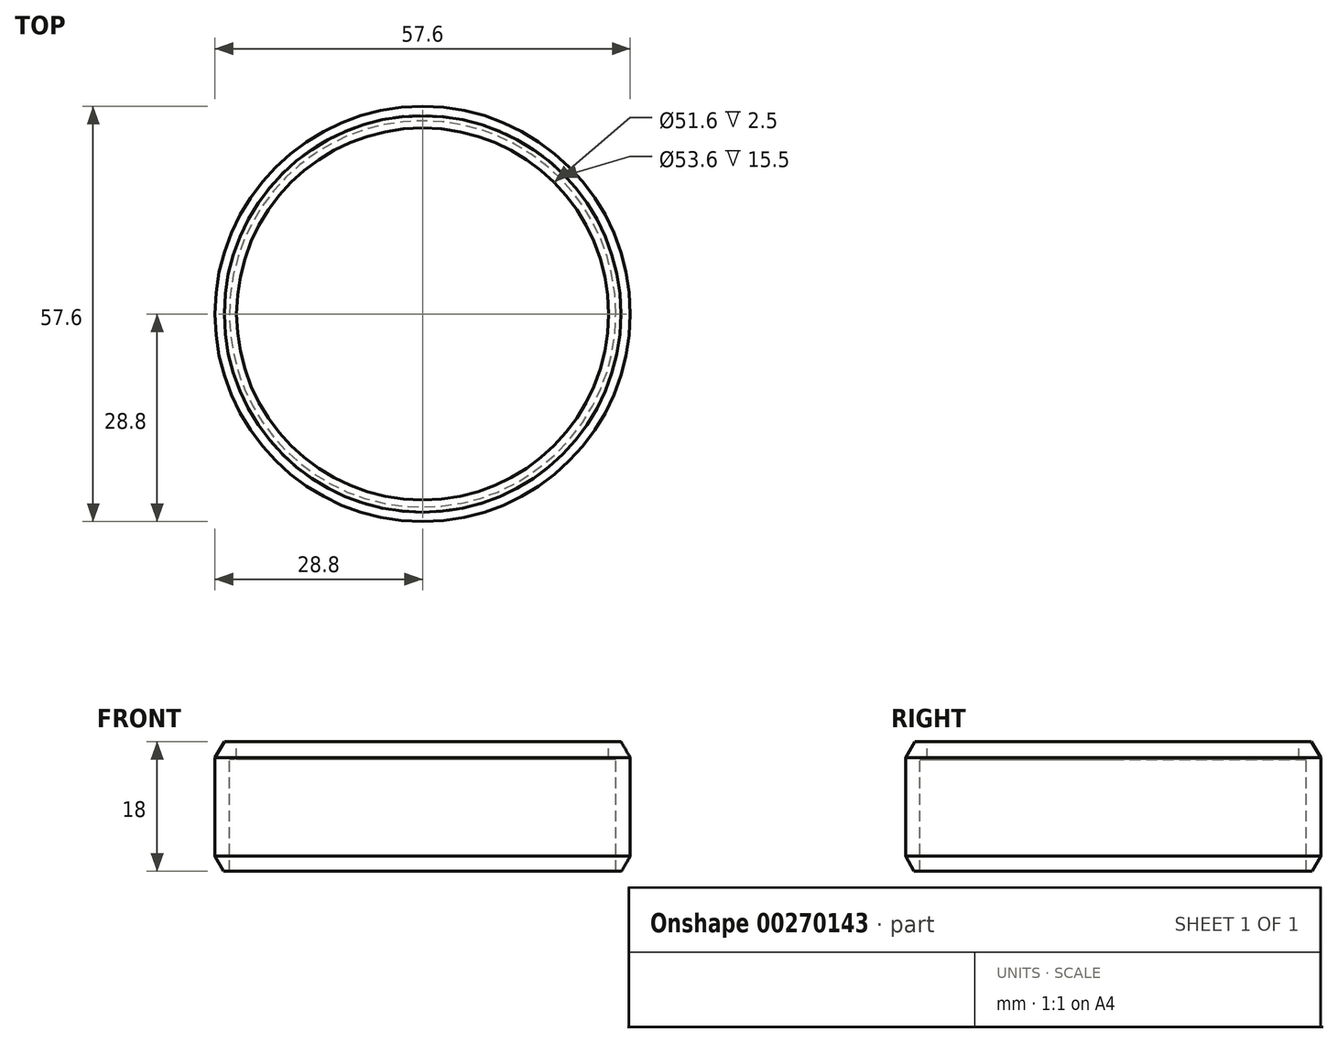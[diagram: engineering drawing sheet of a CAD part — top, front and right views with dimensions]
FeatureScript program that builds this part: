
annotation { "Feature Type Name" : "Feature", "Feature Type Description" : "" }
export const myFeature = defineFeature(function(context is Context, id is Id, definition is map)
    precondition{}
    {
        {
            var Q0;
            Q0=qCreatedBy(makeId("Front.planeOp"),FACE);
            var sketch = newSketch(context, id + "F0", { "sketchPlane" : qUnion([Q0])});
            skLineSegment(sketch, "E0", {"start": v(0, 4.56) * mm, "end": v(0, -3.27) * mm, "construction": true});
            skLineSegment(sketch, "E1.bottom", {"start": v(26.8, 0) * mm, "end": v(27.5, 0) * mm});
            skLineSegment(sketch, "E1.top", {"start": v(26.8, -18) * mm, "end": v(27.6, -18) * mm});
            skLineSegment(sketch, "E1.left", {"start": v(26.8, -2.5) * mm, "end": v(26.8, -18) * mm});
            skLineSegment(sketch, "E1.right", {"start": v(28.8, -2.25) * mm, "end": v(28.8, -15.92) * mm});
            skLineSegment(sketch, "E2", {"start": v(26.8, 0) * mm, "end": v(25.8, 0) * mm});
            skLineSegment(sketch, "E3", {"start": v(25.8, 0) * mm, "end": v(25.8, -2.5) * mm});
            skLineSegment(sketch, "E4", {"start": v(25.8, -2.5) * mm, "end": v(26.8, -2.5) * mm});
            skLineSegment(sketch, "E5", {"start": v(28.8, -2.25) * mm, "end": v(27.5, 0) * mm});
            skLineSegment(sketch, "E6", {"start": v(28.8, -15.92) * mm, "end": v(27.6, -18) * mm});
            skSolve(sketch);
        }
        {
            var Q0;
            Q0=makeQuery(id+"F0.imprint","IMPRINT",FACE,{"disambiguationData":[TD([[makeQuery(id+"F0.imprint","IMPRINT",EDGE,{"derivedFrom":sQuery(id+"F0.wireOp",EDGE,"E1.bottom")}),-1.0]])]});
            var Q1;
            Q1=sQuery(id+"F0.wireOp",EDGE,"E0");
            revolve(context, id + "F1", {"entities" : qUnion([Q0]), "axis" : qUnion([Q1]), "revolveType" : RevolveType.FULL});
        }
    });
